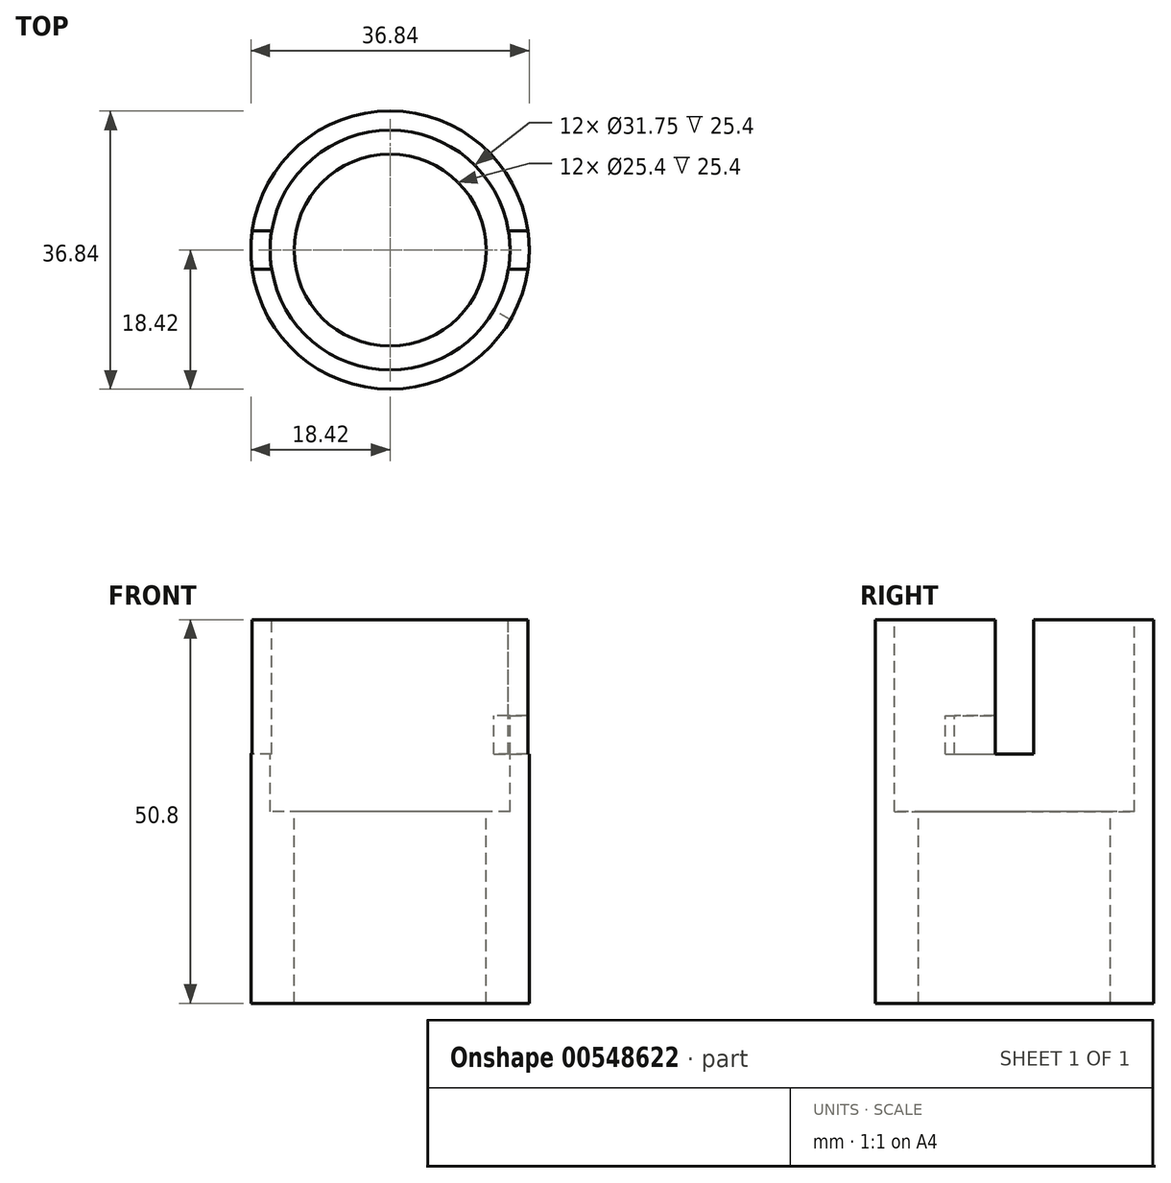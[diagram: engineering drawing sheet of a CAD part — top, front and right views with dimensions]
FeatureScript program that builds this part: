
annotation { "Feature Type Name" : "Feature", "Feature Type Description" : "" }
export const myFeature = defineFeature(function(context is Context, id is Id, definition is map)
    precondition{}
    {
        {
            var Q0;
            Q0=qCreatedBy(makeId("Front.planeOp"),FACE);
            var sketch = newSketch(context, id + "F0", { "sketchPlane" : qUnion([Q0])});
            skLineSegment(sketch, "E0.bottom", {"start": v(15.88, 63.29) * mm, "end": v(18.41, 63.29) * mm});
            skLineSegment(sketch, "E0.top", {"start": v(12.7, 12.49) * mm, "end": v(18.41, 12.49) * mm});
            skLineSegment(sketch, "E0.left", {"start": v(12.7, 37.89) * mm, "end": v(12.7, 12.49) * mm});
            skLineSegment(sketch, "E0.right", {"start": v(18.41, 63.29) * mm, "end": v(18.41, 12.49) * mm});
            skLineSegment(sketch, "E1", {"start": v(15.88, 63.29) * mm, "end": v(15.88, 37.89) * mm});
            skLineSegment(sketch, "E2", {"start": v(15.88, 37.89) * mm, "end": v(12.7, 37.89) * mm});
            skSolve(sketch);
        }
        {
            var Q0;
            Q0=qCreatedBy(makeId("Front.planeOp"),FACE);
            var sketch = newSketch(context, id + "F1", { "sketchPlane" : qUnion([Q0])});
            skLineSegment(sketch, "E3", {"start": v(0, 76.03) * mm, "end": v(0, -80.43) * mm});
            skSolve(sketch);
        }
        {
            var Q0;
            Q0 = qSketchRegion(id + "F0", true);
            var Q1;
            Q1=sQuery(id+"F1.wireOp",EDGE,"E3");
            revolve(context, id + "F2", {"entities" : qUnion([Q0]), "axis" : qUnion([Q1]), "revolveType" : RevolveType.FULL});
        }
        {
            var Q0;
            Q0=qCreatedBy(makeId("Right.planeOp"),FACE);
            var sketch = newSketch(context, id + "F3", { "sketchPlane" : qUnion([Q0])});
            skLineSegment(sketch, "E4.bottom", {"start": v(-2.54, 63.29) * mm, "end": v(0, 63.29) * mm});
            skLineSegment(sketch, "E4.top", {"start": v(-2.54, 45.5) * mm, "end": v(0, 45.5) * mm});
            skLineSegment(sketch, "E4.left", {"start": v(-2.54, 63.29) * mm, "end": v(-2.54, 45.5) * mm});
            skLineSegment(sketch, "E5", {"start": v(0, 63.29) * mm, "end": v(2.54, 63.29) * mm});
            skLineSegment(sketch, "E6", {"start": v(2.54, 63.29) * mm, "end": v(2.54, 45.5) * mm});
            skLineSegment(sketch, "E7", {"start": v(2.54, 45.5) * mm, "end": v(0, 45.5) * mm});
            skSolve(sketch);
        }
        {
            var Q0;
            Q0 = qSketchRegion(id + "F3", true);
            extrude(context, id + "F4", {"entities" : qUnion([Q0]), "operationType" : NewBodyOperationType.REMOVE, "endBound" : BoundingType.SYMMETRIC, "depth" : 50.8 * mm, "offsetDistance" : 25.4 * mm});
        }
        {
            var Q0;
            Q0=qCreatedBy(makeId("Front.planeOp"),FACE);
            var sketch = newSketch(context, id + "F5", { "sketchPlane" : qUnion([Q0])});
            skLineSegment(sketch, "E8.bottom", {"start": v(18.35, 45.5) * mm, "end": v(5.65, 45.5) * mm});
            skLineSegment(sketch, "E8.top", {"start": v(18.35, 50.59) * mm, "end": v(5.65, 50.59) * mm});
            skLineSegment(sketch, "E8.left", {"start": v(18.35, 45.5) * mm, "end": v(18.35, 50.59) * mm});
            skLineSegment(sketch, "E8.right", {"start": v(5.65, 45.5) * mm, "end": v(5.65, 50.59) * mm});
            skSolve(sketch);
        }
        {
            var Q0;
            Q0 = qSketchRegion(id + "F5", true);
            var Q1;
            Q1=makeQuery(id+"F2.opRevolve","SWEPT_FACE",FACE,{"disambiguationData":[OSD([sQuery(id+"F0.wireOp",EDGE,"E0.right")])]});
            revolve(context, id + "F6", {"operationType" : NewBodyOperationType.REMOVE, "entities" : qUnion([Q0]), "axis" : qUnion([Q1]), "revolveType" : RevolveType.ONE_DIRECTION, "oppositeDirection" : true, "angle" : 30 * degree});
        }
    });
